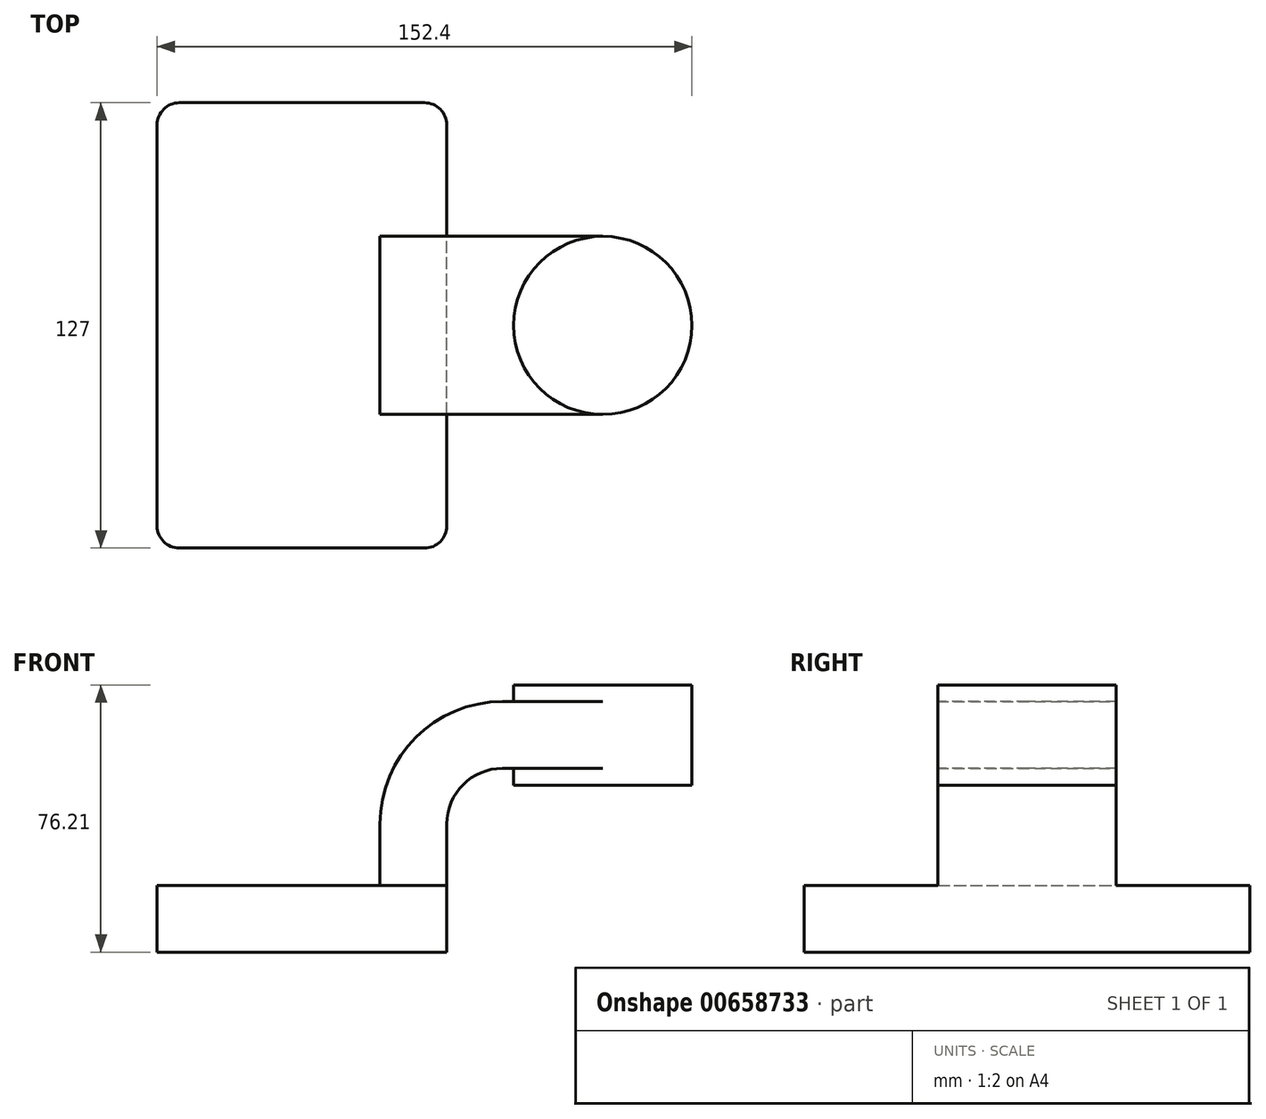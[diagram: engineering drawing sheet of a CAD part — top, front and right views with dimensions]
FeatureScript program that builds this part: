
annotation { "Feature Type Name" : "Feature", "Feature Type Description" : "" }
export const myFeature = defineFeature(function(context is Context, id is Id, definition is map)
    precondition{}
    {
        {
            var Q0;
            Q0=qCreatedBy(makeId("Front.planeOp"),FACE);
            var sketch = newSketch(context, id + "F0", { "sketchPlane" : qUnion([Q0])});
            skLineSegment(sketch, "E0.bottom", {"start": v(-41.27, -9.53) * mm, "end": v(41.28, -9.53) * mm});
            skLineSegment(sketch, "E0.top", {"start": v(-41.28, 9.52) * mm, "end": v(41.28, 9.52) * mm});
            skLineSegment(sketch, "E0.left", {"start": v(-41.28, -9.53) * mm, "end": v(-41.28, 9.52) * mm});
            skLineSegment(sketch, "E0.right", {"start": v(41.28, -9.53) * mm, "end": v(41.28, 9.52) * mm});
            skPoint(sketch, "E0.middle", {"position": v(0, 0) * mm});
            skLineSegment(sketch, "E1.bottom", {"start": v(111.13, 66.67) * mm, "end": v(60.32, 66.67) * mm});
            skLineSegment(sketch, "E1.top", {"start": v(111.12, 38.1) * mm, "end": v(60.32, 38.1) * mm});
            skLineSegment(sketch, "E1.left", {"start": v(111.12, 66.67) * mm, "end": v(111.12, 38.1) * mm});
            skLineSegment(sketch, "E1.right", {"start": v(60.33, 66.67) * mm, "end": v(60.32, 38.1) * mm});
            skPoint(sketch, "E1.middle", {"position": v(85.72, 52.39) * mm});
            skLineSegment(sketch, "E2", {"start": v(41.28, 9.52) * mm, "end": v(41.28, 27) * mm});
            skArc(sketch, "E3", {"start": v(41.27, 27) * mm, "mid": v(45.92, 38.23) * mm, "end": v(57.15, 42.88) * mm});
            skLineSegment(sketch, "E4", {"start": v(57.15, 42.88) * mm, "end": v(85.73, 42.88) * mm});
            skArc(sketch, "E5.1", {"start": v(22.22, 27) * mm, "mid": v(32.45, 51.7) * mm, "end": v(57.15, 61.93) * mm});
            skLineSegment(sketch, "E5.2", {"start": v(22.22, 9.52) * mm, "end": v(22.22, 27) * mm});
            skLineSegment(sketch, "E6", {"start": v(85.73, 38.1) * mm, "end": v(85.73, 66.68) * mm});
            skFitSpline(sketch, "E7", {"points": [v(-41.28, 9.53) * mm, v(57.15, 61.93) * mm], "startDerivative": vector(-0.6, 61.63) * mm, "endDerivative": vector(125.61, -0.25) * mm});
            skLineSegment(sketch, "E8", {"start": v(57.15, 61.93) * mm, "end": v(85.73, 61.93) * mm});
            skSolve(sketch);
        }
        {
            var Q0;
            Q0=makeQuery(id+"F0.imprint","IMPRINT",FACE,{"disambiguationData":[TD([[makeQuery(id+"F0.imprint","IMPRINT",EDGE,{"derivedFrom":sQuery(id+"F0.wireOp",EDGE,"E0.bottom")}),1.0]])]});
            extrude(context, id + "F1", {"entities" : qUnion([Q0]), "endBound" : BoundingType.SYMMETRIC, "depth" : 127 * mm, "offsetDistance" : 25.4 * mm});
        }
        {
            var Q0;
            {var subQ1=sQuery(id+"F0.wireOp",EDGE,"E2");Q0=makeQuery(id+"F0.imprint","IMPRINT",FACE,{"disambiguationData":[TD([[makeQuery(id+"F0.imprint","IMPRINT",EDGE,{"derivedFrom":subQ1}),1.0]])]});}
            var Q1;
            {var subQ0=sQuery(id+"F0.wireOp",EDGE,"E8");var subQ1=sQuery(id+"F0.wireOp",EDGE,"E1.right");var subQ2=makeQuery(id+"F0.imprint","INTERSECT",VERTEX,{"derivedFrom":[subQ1,subQ0]});Q1=makeQuery(id+"F0.imprint","IMPRINT",FACE,{"disambiguationData":[TD([[makeQuery(id+"F0.imprint","IMPRINT",EDGE,{"disambiguationData":[TD([[subQ2,-1.0]])],"derivedFrom":subQ1}),1.0]])]});}
            extrude(context, id + "F2", {"entities" : qUnion([Q0, Q1]), "operationType" : NewBodyOperationType.ADD, "endBound" : BoundingType.SYMMETRIC, "depth" : 50.8 * mm, "offsetDistance" : 25.4 * mm});
        }
        {
            var Q0;
            Q0=makeQuery(id+"F0.imprint","IMPRINT",FACE,{"disambiguationData":[TD([[makeQuery(id+"F0.imprint","IMPRINT",EDGE,{"derivedFrom":sQuery(id+"F0.wireOp",EDGE,"E5.1")}),1.0]])]});
            extrude(context, id + "F3", {"entities" : qUnion([Q0]), "operationType" : NewBodyOperationType.ADD, "endBound" : BoundingType.SYMMETRIC, "depth" : 19.05 * mm, "offsetDistance" : 25.4 * mm});
        }
        {
            var Q0;
            {var subQ4=sQuery(id+"F0.wireOp",EDGE,"E1.left");Q0=makeQuery(id+"F0.imprint","IMPRINT",FACE,{"disambiguationData":[TD([[makeQuery(id+"F0.imprint","IMPRINT",EDGE,{"derivedFrom":subQ4}),-1.0]])]});}
            var Q1;
            Q1=sQuery(id+"F0.wireOp",EDGE,"E6");
            revolve(context, id + "F4", {"operationType" : NewBodyOperationType.ADD, "entities" : qUnion([Q0]), "axis" : qUnion([Q1]), "revolveType" : RevolveType.FULL});
        }
        {
            var Q0;
            Q0=makeQuery(id+"F1.opExtrude","CAP_EDGE",EDGE,{"disambiguationData":[OSD([sQuery(id+"F0.wireOp",EDGE,"E0.right")])],"isStart":false});
            var Q1;
            Q1=makeQuery(id+"F1.opExtrude","CAP_EDGE",EDGE,{"disambiguationData":[OSD([sQuery(id+"F0.wireOp",EDGE,"E0.left")])],"isStart":false});
            var Q2;
            Q2=makeQuery(id+"F1.opExtrude","CAP_EDGE",EDGE,{"disambiguationData":[OSD([sQuery(id+"F0.wireOp",EDGE,"E0.right")])],"isStart":true});
            var Q3;
            Q3=makeQuery(id+"F1.opExtrude","CAP_EDGE",EDGE,{"disambiguationData":[OSD([sQuery(id+"F0.wireOp",EDGE,"E0.left")])],"isStart":true});
            fillet(context, id + "F5", {"entities" : qUnion([Q0, Q1, Q2, Q3]), "radius" : 6.35 * mm, "tangentPropagation" : true, "allowEdgeOverflow" : false});
        }
    });
